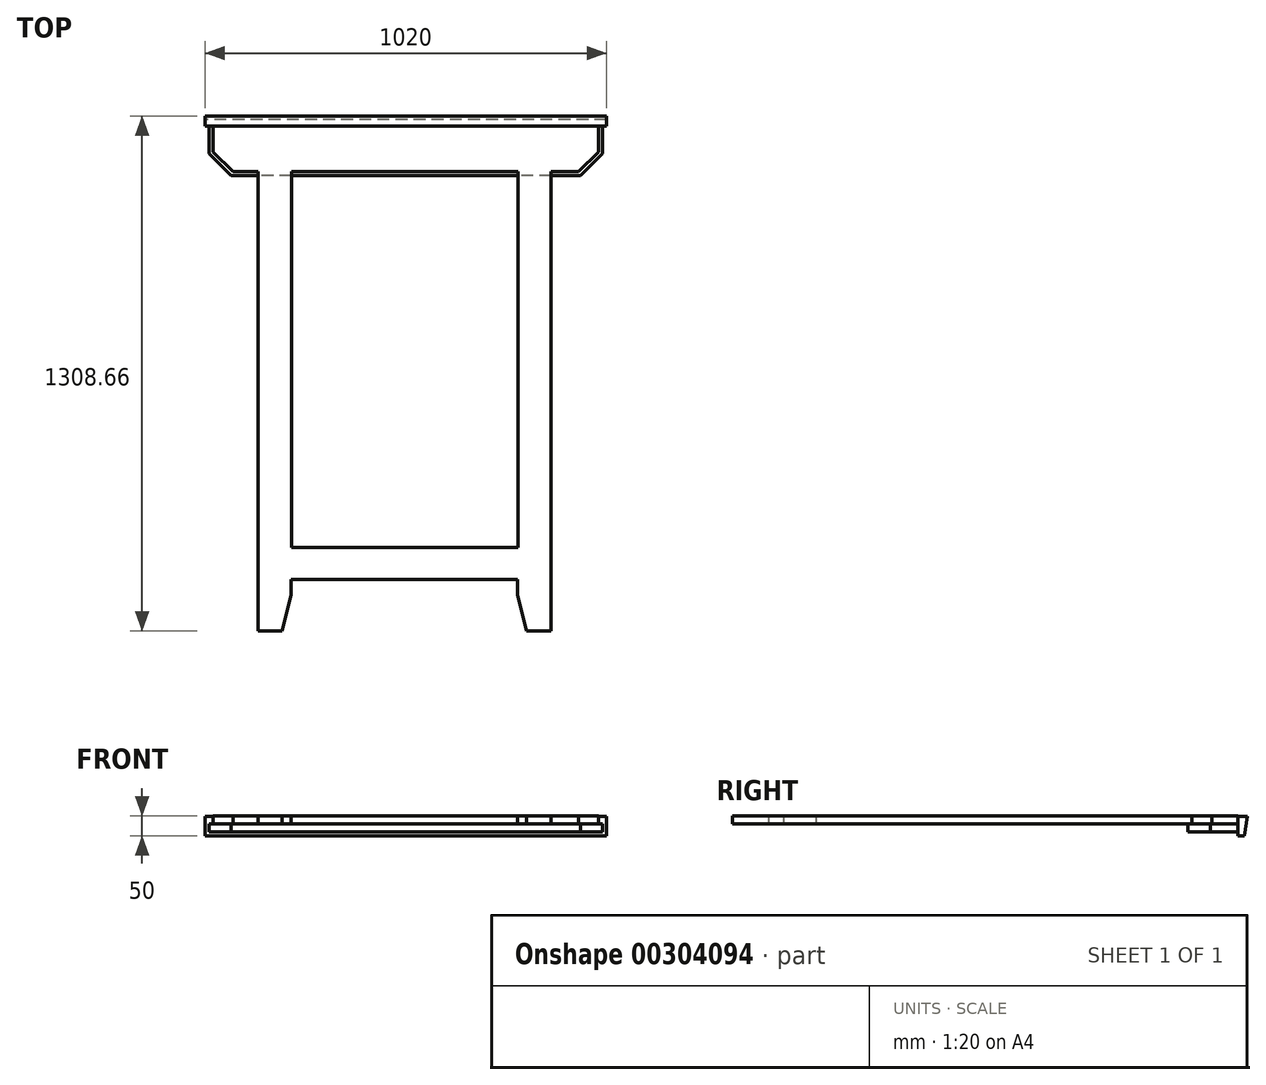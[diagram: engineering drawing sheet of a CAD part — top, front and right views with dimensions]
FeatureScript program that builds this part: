
annotation { "Feature Type Name" : "Feature", "Feature Type Description" : "" }
export const myFeature = defineFeature(function(context is Context, id is Id, definition is map)
    precondition{}
    {
        {
            var Q0;
            Q0=qCreatedBy(makeId("Top.planeOp"),FACE);
            var sketch = newSketch(context, id + "F0", { "sketchPlane" : qUnion([Q0])});
            skLineSegment(sketch, "E0", {"start": v(-503.02, 109.35) * mm, "end": v(496.98, 109.35) * mm});
            skLineSegment(sketch, "E1", {"start": v(496.98, 109.35) * mm, "end": v(496.98, 39.35) * mm});
            skLineSegment(sketch, "E2", {"start": v(496.98, 39.35) * mm, "end": v(440.42, -17.22) * mm});
            skLineSegment(sketch, "E3", {"start": v(440.42, -17.22) * mm, "end": v(-446.45, -17.22) * mm});
            skLineSegment(sketch, "E4", {"start": v(-446.45, -17.22) * mm, "end": v(-503.02, 39.35) * mm});
            skLineSegment(sketch, "E5", {"start": v(-503.02, 39.35) * mm, "end": v(-503.02, 109.35) * mm});
            skSolve(sketch);
        }
        {
            var Q0;
            Q0=makeQuery(id+"F0.imprint","IMPRINT",FACE,{"disambiguationData":[TD([[makeQuery(id+"F0.imprint","IMPRINT",EDGE,{"derivedFrom":sQuery(id+"F0.wireOp",EDGE,"E0")}),-1.0]])]});
            extrude(context, id + "F1", {"entities" : qUnion([Q0]), "depth" : 20 * mm, "offsetDistance" : 25 * mm});
        }
        {
            var Q0;
            Q0=makeQuery(id+"F1.opExtrude","CAP_FACE",FACE,{"disambiguationData":[OSD([sQuery(id+"F0.wireOp",EDGE,"E0"),sQuery(id+"F0.wireOp",EDGE,"E1"),sQuery(id+"F0.wireOp",EDGE,"E2"),sQuery(id+"F0.wireOp",EDGE,"E3"),sQuery(id+"F0.wireOp",EDGE,"E4"),sQuery(id+"F0.wireOp",EDGE,"E5")])],"isStart":false});
            var sketch = newSketch(context, id + "F2", { "sketchPlane" : qUnion([Q0])});
            skLineSegment(sketch, "E6.0", {"start": v(-493.02, 43.5) * mm, "end": v(-493.02, 99.35) * mm});
            skLineSegment(sketch, "E6.1", {"start": v(486.98, 99.35) * mm, "end": v(486.98, 43.5) * mm});
            skLineSegment(sketch, "E6.2", {"start": v(486.98, 43.5) * mm, "end": v(436.27, -7.22) * mm});
            skLineSegment(sketch, "E6.3", {"start": v(-493.02, 99.35) * mm, "end": v(486.98, 99.35) * mm});
            skLineSegment(sketch, "E6.4", {"start": v(436.27, -7.22) * mm, "end": v(-442.3, -7.22) * mm});
            skLineSegment(sketch, "E6.5", {"start": v(-442.3, -7.22) * mm, "end": v(-493.02, 43.5) * mm});
            skSolve(sketch);
        }
        {
            var Q0;
            Q0=makeQuery(id+"F2.imprint","IMPRINT",FACE,{"disambiguationData":[TD([[makeQuery(id+"F2.imprint","IMPRINT",EDGE,{"derivedFrom":sQuery(id+"F2.wireOp",EDGE,"E6.0")}),-1.0]])]});
            extrude(context, id + "F3", {"entities" : qUnion([Q0]), "operationType" : NewBodyOperationType.ADD, "depth" : 20 * mm, "offsetDistance" : 25 * mm});
        }
        {
            var Q0;
            Q0=makeQuery(id+"F3.opExtrude","SWEPT_FACE",FACE,{"disambiguationData":[OSD([sQuery(id+"F2.wireOp",EDGE,"E6.3")])]});
            extrude(context, id + "F4", {"entities" : qUnion([Q0]), "operationType" : NewBodyOperationType.ADD, "depth" : 10 * mm, "offsetDistance" : 25 * mm});
        }
        {
            var Q0;
            {var subQ0=sQuery(id+"F2.wireOp",EDGE,"E6.3");Q0=makeQuery(id+"F4.boolean.opBoolean","MERGE",FACE,{"derivedFrom":[makeQuery(id+"F3.opExtrude","CAP_FACE",FACE,{"disambiguationData":[OSD([sQuery(id+"F2.wireOp",EDGE,"E6.0"),sQuery(id+"F2.wireOp",EDGE,"E6.1"),sQuery(id+"F2.wireOp",EDGE,"E6.2"),subQ0,sQuery(id+"F2.wireOp",EDGE,"E6.4"),sQuery(id+"F2.wireOp",EDGE,"E6.5")])],"isStart":false}),makeQuery(id+"F4.opExtrude","SWEPT_FACE",FACE,{"disambiguationData":[OSD([subQ0]),TDD([makeQuery(id+"F3.opExtrude","CAP_EDGE",EDGE,{"disambiguationData":[OSD([subQ0])],"isStart":false})])]})]});}
            var sketch = newSketch(context, id + "F5", { "sketchPlane" : qUnion([Q0])});
            skLineSegment(sketch, "E7", {"start": v(-377.82, -7.22) * mm, "end": v(-377.82, -1174.3) * mm});
            skLineSegment(sketch, "E8", {"start": v(-377.82, -1174.3) * mm, "end": v(-317.18, -1174.3) * mm});
            skLineSegment(sketch, "E9", {"start": v(-317.18, -1174.3) * mm, "end": v(-294.1, -1082.02) * mm});
            skLineSegment(sketch, "E10", {"start": v(-294.1, -1082.02) * mm, "end": v(-294.1, -1043.52) * mm});
            skLineSegment(sketch, "E11", {"start": v(-294.1, -1043.52) * mm, "end": v(281.09, -1043.52) * mm});
            skLineSegment(sketch, "E12", {"start": v(281.09, -1043.52) * mm, "end": v(281.09, -1082.02) * mm});
            skLineSegment(sketch, "E13", {"start": v(281.09, -1082.02) * mm, "end": v(304.16, -1174.3) * mm});
            skLineSegment(sketch, "E14", {"start": v(304.16, -1174.3) * mm, "end": v(366.42, -1174.3) * mm});
            skLineSegment(sketch, "E15", {"start": v(366.42, -1174.3) * mm, "end": v(366.42, -7.22) * mm});
            skLineSegment(sketch, "E16", {"start": v(366.42, -7.22) * mm, "end": v(281.9, -7.22) * mm});
            skLineSegment(sketch, "E17", {"start": v(281.9, -7.22) * mm, "end": v(281.9, -961.44) * mm});
            skLineSegment(sketch, "E18", {"start": v(281.9, -961.44) * mm, "end": v(-293.3, -961.44) * mm});
            skLineSegment(sketch, "E19", {"start": v(-293.3, -961.44) * mm, "end": v(-293.3, -7.22) * mm});
            skLineSegment(sketch, "E20", {"start": v(-293.3, -7.22) * mm, "end": v(-377.82, -7.22) * mm});
            skSolve(sketch);
        }
        {
            var Q0;
            Q0=makeQuery(id+"F5.imprint","IMPRINT",FACE,{"disambiguationData":[TD([[makeQuery(id+"F5.imprint","IMPRINT",EDGE,{"derivedFrom":sQuery(id+"F5.wireOp",EDGE,"E7")}),1.0]])]});
            extrude(context, id + "F6", {"entities" : qUnion([Q0]), "operationType" : NewBodyOperationType.ADD, "oppositeDirection" : true, "depth" : 20 * mm, "offsetDistance" : 25 * mm});
        }
        {
            var Q0;
            Q0=makeQuery(id+"F4.boolean.opBoolean","MERGE",FACE,{"derivedFrom":[makeQuery(id+"F1.opExtrude","SWEPT_FACE",FACE,{"disambiguationData":[OSD([sQuery(id+"F0.wireOp",EDGE,"E0")])]}),makeQuery(id+"F4.opExtrude","CAP_FACE",FACE,{"disambiguationData":[OSD([sQuery(id+"F2.wireOp",EDGE,"E6.3")])],"isStart":false})]});
            var sketch = newSketch(context, id + "F7", { "sketchPlane" : qUnion([Q0])});
            skLineSegment(sketch, "E21.bottom", {"start": v(-496.98, 0) * mm, "end": v(503.3, 0) * mm});
            skLineSegment(sketch, "E21.top", {"start": v(-496.98, 39.77) * mm, "end": v(503.3, 39.77) * mm});
            skLineSegment(sketch, "E21.left", {"start": v(-496.98, 0) * mm, "end": v(-496.98, 39.77) * mm});
            skLineSegment(sketch, "E21.right", {"start": v(503.3, 0) * mm, "end": v(503.3, 39.77) * mm});
            skSolve(sketch);
        }
        {
            var Q0;
            {var subQ0=sQuery(id+"F7.wireOp",EDGE,"E21.left");var subQ1=sQuery(id+"F7.wireOp",EDGE,"E21.top");var subQ2=makeQuery(id+"F7.imprint","INTERSECT",VERTEX,{"derivedFrom":[subQ1,subQ0]});Q0=makeQuery(id+"F7.imprint","IMPRINT",FACE,{"disambiguationData":[TD([[makeQuery(id+"F7.imprint","IMPRINT",EDGE,{"disambiguationData":[TD([[subQ2,-1.0]])],"derivedFrom":subQ1}),-1.0]])]});}
            var Q1;
            {var subQ0=sQuery(id+"F0.wireOp",EDGE,"E5");var subQ1=sQuery(id+"F0.wireOp",EDGE,"E0");var subQ2=makeQuery(id+"F1.opExtrude","SWEPT_EDGE",EDGE,{"disambiguationData":[OSD([subQ1,subQ0])]});Q1=makeQuery(id+"F7.imprint","IMPRINT",FACE,{"disambiguationData":[TD([[makeQuery(id+"F7.imprint","IMPRINT",EDGE,{"derivedFrom":subQ2}),-1.0]])]});}
            extrude(context, id + "F8", {"entities" : qUnion([Q0, Q1]), "operationType" : NewBodyOperationType.ADD, "depth" : 25 * mm, "offsetDistance" : 25 * mm});
        }
        {
            var Q0;
            Q0=makeQuery(id+"F8.boolean.opBoolean","MERGE",FACE,{"derivedFrom":[makeQuery(id+"F1.opExtrude","SWEPT_FACE",FACE,{"disambiguationData":[OSD([sQuery(id+"F0.wireOp",EDGE,"E1")])]}),makeQuery(id+"F8.opExtrude","SWEPT_FACE",FACE,{"disambiguationData":[OSD([sQuery(id+"F7.wireOp",EDGE,"E21.left")])]})]});
            var sketch = newSketch(context, id + "F9", { "sketchPlane" : qUnion([Q0])});
            skLineSegment(sketch, "E22.bottom", {"start": v(109.35, 39.77) * mm, "end": v(134.35, 39.77) * mm});
            skLineSegment(sketch, "E22.top", {"start": v(109.35, 0) * mm, "end": v(134.35, 0) * mm});
            skLineSegment(sketch, "E22.left", {"start": v(109.35, 39.77) * mm, "end": v(109.35, 0) * mm});
            skLineSegment(sketch, "E22.right", {"start": v(134.35, 39.77) * mm, "end": v(134.35, 0) * mm});
            skSolve(sketch);
        }
        {
            var Q0;
            {var subQ1=sQuery(id+"F9.wireOp",EDGE,"E22.bottom");Q0=makeQuery(id+"F9.imprint","IMPRINT",FACE,{"disambiguationData":[TD([[makeQuery(id+"F9.imprint","IMPRINT",EDGE,{"derivedFrom":subQ1}),1.0]])]});}
            extrude(context, id + "F10", {"entities" : qUnion([Q0]), "operationType" : NewBodyOperationType.ADD, "depth" : 10 * mm, "offsetDistance" : 25 * mm});
        }
        {
            var Q0;
            {var subQ0=sQuery(id+"F2.wireOp",EDGE,"E6.3");var subQ1=sQuery(id+"F2.wireOp",EDGE,"E6.0");Q0=makeQuery(id+"F8.boolean.opBoolean","MERGE",FACE,{"derivedFrom":[makeQuery(id+"F4.boolean.opBoolean","MERGE",FACE,{"derivedFrom":[makeQuery(id+"F3.opExtrude","SWEPT_FACE",FACE,{"disambiguationData":[OSD([subQ1])]}),makeQuery(id+"F4.opExtrude","SWEPT_FACE",FACE,{"disambiguationData":[OSD([subQ1,subQ0])]})]}),makeQuery(id+"F8.opExtrude","SWEPT_FACE",FACE,{"disambiguationData":[OSD([subQ1,subQ0])]})]});}
            var sketch = newSketch(context, id + "F11", { "sketchPlane" : qUnion([Q0])});
            skLineSegment(sketch, "E23.bottom", {"start": v(-109.35, 40) * mm, "end": v(-134.35, 40) * mm});
            skLineSegment(sketch, "E23.top", {"start": v(-109.35, 0) * mm, "end": v(-134.35, 0) * mm});
            skLineSegment(sketch, "E23.left", {"start": v(-109.35, 40) * mm, "end": v(-109.35, 0) * mm});
            skLineSegment(sketch, "E23.right", {"start": v(-134.35, 40) * mm, "end": v(-134.35, 0) * mm});
            skSolve(sketch);
        }
        {
            var Q0;
            {var subQ1=sQuery(id+"F2.wireOp",EDGE,"E6.3");var subQ2=sQuery(id+"F2.wireOp",EDGE,"E6.0");var subQ3=makeQuery(id+"F8.opExtrude","SWEPT_EDGE",EDGE,{"disambiguationData":[OSD([subQ2,subQ1,sQuery(id+"F7.wireOp",EDGE,"E21.top")])]});Q0=makeQuery(id+"F11.imprint","IMPRINT",FACE,{"disambiguationData":[TD([[makeQuery(id+"F11.imprint","IMPRINT",EDGE,{"derivedFrom":subQ3}),-1.0]])]});}
            var Q1;
            {var subQ0=sQuery(id+"F11.wireOp",EDGE,"E23.top");Q1=makeQuery(id+"F11.imprint","IMPRINT",FACE,{"disambiguationData":[TD([[makeQuery(id+"F11.imprint","IMPRINT",EDGE,{"derivedFrom":subQ0}),-1.0]])]});}
            extrude(context, id + "F12", {"entities" : qUnion([Q0, Q1]), "operationType" : NewBodyOperationType.ADD, "depth" : 20 * mm, "offsetDistance" : 25 * mm});
        }
        {
            var Q0;
            Q0=makeQuery(id+"F12.boolean.opBoolean","MERGE",FACE,{"derivedFrom":[makeQuery(id+"F10.boolean.opBoolean","MERGE",FACE,{"derivedFrom":[makeQuery(id+"F8.boolean.opBoolean","MERGE",FACE,{"derivedFrom":[makeQuery(id+"F1.opExtrude","CAP_FACE",FACE,{"disambiguationData":[OSD([sQuery(id+"F0.wireOp",EDGE,"E0"),sQuery(id+"F0.wireOp",EDGE,"E1"),sQuery(id+"F0.wireOp",EDGE,"E2"),sQuery(id+"F0.wireOp",EDGE,"E3"),sQuery(id+"F0.wireOp",EDGE,"E4"),sQuery(id+"F0.wireOp",EDGE,"E5")])],"isStart":true}),makeQuery(id+"F8.opExtrude","SWEPT_FACE",FACE,{"disambiguationData":[OSD([sQuery(id+"F7.wireOp",EDGE,"E21.bottom")])]})]}),makeQuery(id+"F10.opExtrude","SWEPT_FACE",FACE,{"disambiguationData":[OSD([sQuery(id+"F9.wireOp",EDGE,"E22.top")])]})]}),makeQuery(id+"F12.opExtrude","SWEPT_FACE",FACE,{"disambiguationData":[OSD([sQuery(id+"F11.wireOp",EDGE,"E23.top")])]})]});
            var sketch = newSketch(context, id + "F13", { "sketchPlane" : qUnion([Q0])});
            skLineSegment(sketch, "E24.bottom", {"start": v(506.98, -134.35) * mm, "end": v(-513.02, -134.35) * mm});
            skLineSegment(sketch, "E24.top", {"start": v(506.98, -109.35) * mm, "end": v(-513.02, -109.35) * mm});
            skLineSegment(sketch, "E24.left", {"start": v(506.98, -134.35) * mm, "end": v(506.98, -109.35) * mm});
            skLineSegment(sketch, "E24.right", {"start": v(-513.02, -134.35) * mm, "end": v(-513.02, -109.35) * mm});
            skSolve(sketch);
        }
        {
            var Q0;
            Q0=makeQuery(id+"F13.imprint","IMPRINT",FACE,{"disambiguationData":[TD([[makeQuery(id+"F13.imprint","IMPRINT",EDGE,{"derivedFrom":sQuery(id+"F13.wireOp",EDGE,"E24.bottom")}),1.0]])]});
            extrude(context, id + "F14", {"entities" : qUnion([Q0]), "operationType" : NewBodyOperationType.ADD, "depth" : 10 * mm, "offsetDistance" : 25 * mm});
        }
        {
            var Q0;
            Q0=makeQuery(id+"F14.boolean.opBoolean","MERGE",FACE,{"derivedFrom":[makeQuery(id+"F12.opExtrude","CAP_FACE",FACE,{"disambiguationData":[OSD([sQuery(id+"F2.wireOp",EDGE,"E6.0"),sQuery(id+"F2.wireOp",EDGE,"E6.3"),sQuery(id+"F7.wireOp",EDGE,"E21.top"),sQuery(id+"F11.wireOp",EDGE,"E23.top"),sQuery(id+"F11.wireOp",EDGE,"E23.left"),sQuery(id+"F11.wireOp",EDGE,"E23.right")])],"isStart":false}),makeQuery(id+"F14.opExtrude","SWEPT_FACE",FACE,{"disambiguationData":[OSD([sQuery(id+"F13.wireOp",EDGE,"E24.right")])]})]});
            var sketch = newSketch(context, id + "F15", { "sketchPlane" : qUnion([Q0])});
            skLineSegment(sketch, "E25", {"start": v(-134.35, -10) * mm, "end": v(-134.35, 39.77) * mm});
            skLineSegment(sketch, "E26", {"start": v(-134.35, 39.77) * mm, "end": v(-125.9, -10) * mm});
            skLineSegment(sketch, "E27", {"start": v(-125.9, -10) * mm, "end": v(-134.35, -10) * mm});
            skSolve(sketch);
        }
        {
            var Q0;
            Q0=makeQuery(id+"F15.imprint","IMPRINT",FACE,{"disambiguationData":[TD([[makeQuery(id+"F15.imprint","IMPRINT",EDGE,{"derivedFrom":sQuery(id+"F15.wireOp",EDGE,"E25")}),1.0]])]});
            extrude(context, id + "F16", {"entities" : qUnion([Q0]), "operationType" : NewBodyOperationType.REMOVE, "endBound" : BoundingType.THROUGH_ALL, "oppositeDirection" : true, "depth" : 25 * mm, "offsetDistance" : 25 * mm});
        }
    });
